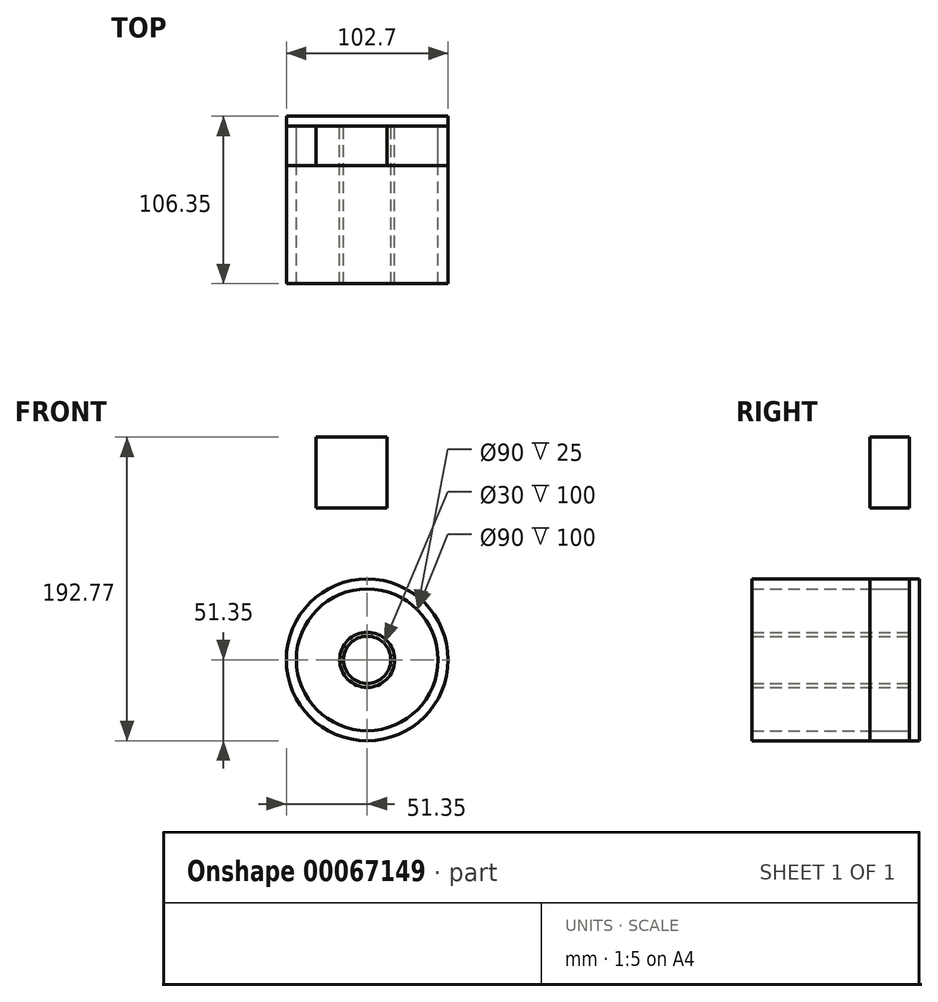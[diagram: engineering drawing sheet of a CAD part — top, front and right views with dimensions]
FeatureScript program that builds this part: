
annotation { "Feature Type Name" : "Feature", "Feature Type Description" : "" }
export const myFeature = defineFeature(function(context is Context, id is Id, definition is map)
    precondition{}
    {
        {
            var Q0;
            Q0=qCreatedBy(makeId("Front.planeOp"),FACE);
            var sketch = newSketch(context, id + "F0", { "sketchPlane" : qUnion([Q0])});
            skCircle(sketch, "E0", {"center": v(0, 0) * mm, "radius": 45 * mm});
            skCircle(sketch, "E1", {"center": v(0, 0) * mm, "radius": 51.35 * mm});
            skCircle(sketch, "E2", {"center": v(0, 0) * mm, "radius": 15 * mm});
            skLineSegment(sketch, "E3.rect.bottom", {"start": v(12.63, 96.42) * mm, "end": v(-32.37, 96.42) * mm});
            skLineSegment(sketch, "E3.rect.top", {"start": v(12.63, 141.42) * mm, "end": v(-32.37, 141.42) * mm});
            skLineSegment(sketch, "E3.rect.left", {"start": v(12.63, 96.42) * mm, "end": v(12.63, 141.42) * mm});
            skLineSegment(sketch, "E3.rect.right", {"start": v(-32.37, 96.42) * mm, "end": v(-32.37, 141.42) * mm});
            skPoint(sketch, "E3.rect.middle", {"position": v(-9.87, 118.92) * mm});
            skCircle(sketch, "E4", {"center": v(0, 0) * mm, "radius": 17.5 * mm});
            skSolve(sketch);
        }
        {
            var Q0;
            Q0=makeQuery(id+"F0.imprint","IMPRINT",FACE,{"disambiguationData":[TD([[makeQuery(id+"F0.imprint","IMPRINT",EDGE,{"derivedFrom":sQuery(id+"F0.wireOp",EDGE,"E2")}),-1.0]])]});
            var Q1;
            Q1=makeQuery(id+"F0.imprint","IMPRINT",FACE,{"disambiguationData":[TD([[makeQuery(id+"F0.imprint","IMPRINT",EDGE,{"derivedFrom":sQuery(id+"F0.wireOp",EDGE,"E0")}),-1.0]])]});
            extrude(context, id + "F1", {"entities" : qUnion([Q0, Q1]), "depth" : 100 * mm});
        }
        {
            var Q0;
            Q0=qCreatedBy(makeId("Front.planeOp"),FACE);
            var sketch = newSketch(context, id + "F2", { "sketchPlane" : qUnion([Q0])});
            skCircle(sketch, "E5", {"center": v(0, 0) * mm, "radius": 51.35 * mm});
            skSolve(sketch);
        }
        {
            var Q0;
            Q0=makeQuery(id+"F2.imprint","IMPRINT",FACE,{"disambiguationData":[TD([[makeQuery(id+"F2.imprint","IMPRINT",EDGE,{"derivedFrom":sQuery(id+"F2.wireOp",EDGE,"E5")}),1.0]])]});
            extrude(context, id + "F3", {"entities" : qUnion([Q0]), "oppositeDirection" : true, "depth" : 6.35 * mm});
        }
        {
            var Q0;
            Q0 = qSketchRegion(id + "F0", true);
            extrude(context, id + "F4", {"entities" : qUnion([Q0]), "depth" : 25 * mm});
        }
    });
